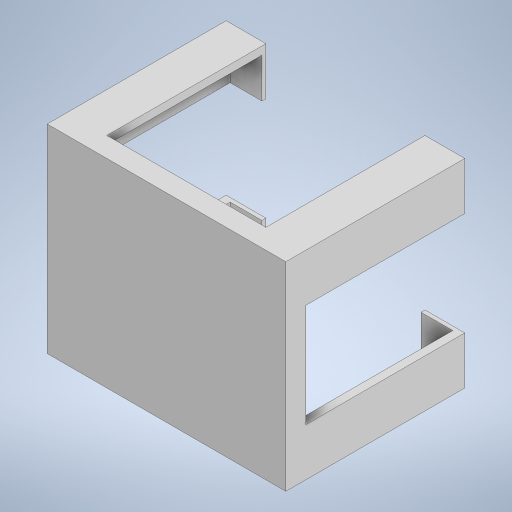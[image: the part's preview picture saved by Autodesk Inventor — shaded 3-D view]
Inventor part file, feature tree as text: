
AUTODESK INVENTOR PART (.ipt)
format: ipt  version: 2024 (Build 280153000, 153)  size: 277,504 bytes
history: native  units: mm
features: extrude x3, sketch x2, other x1, projected_geometry x1
ambient origin geometry x8: Origin, YZ Plane, XZ Plane, XY Plane, X Axis, Y Axis, Z Axis, Center Point
bodies: Body1 (feature_tree)
feature tree (7):
  other  "Sólido1"
  sketch  "Boceto1"  dims[d0=600.0mm d1=500.0mm]
  extrude  "Extrusión1"  Depth=500.0mm
  extrude  "Extrusión2"  Depth=100.0mm
  extrude  "Extrusión3"  Depth=10.0mm
  sketch  "Boceto2"  dims[d4=20.0mm d5=100.0mm d6=60.0mm d7=50.0mm d8=0.0mm d9=50.0mm d10=390.0mm d11=0.0mm d12=0.0mm d13=20.0mm d14=10.0mm d15=0.0mm]
  projected_geometry  "Contorno proyectado1"
